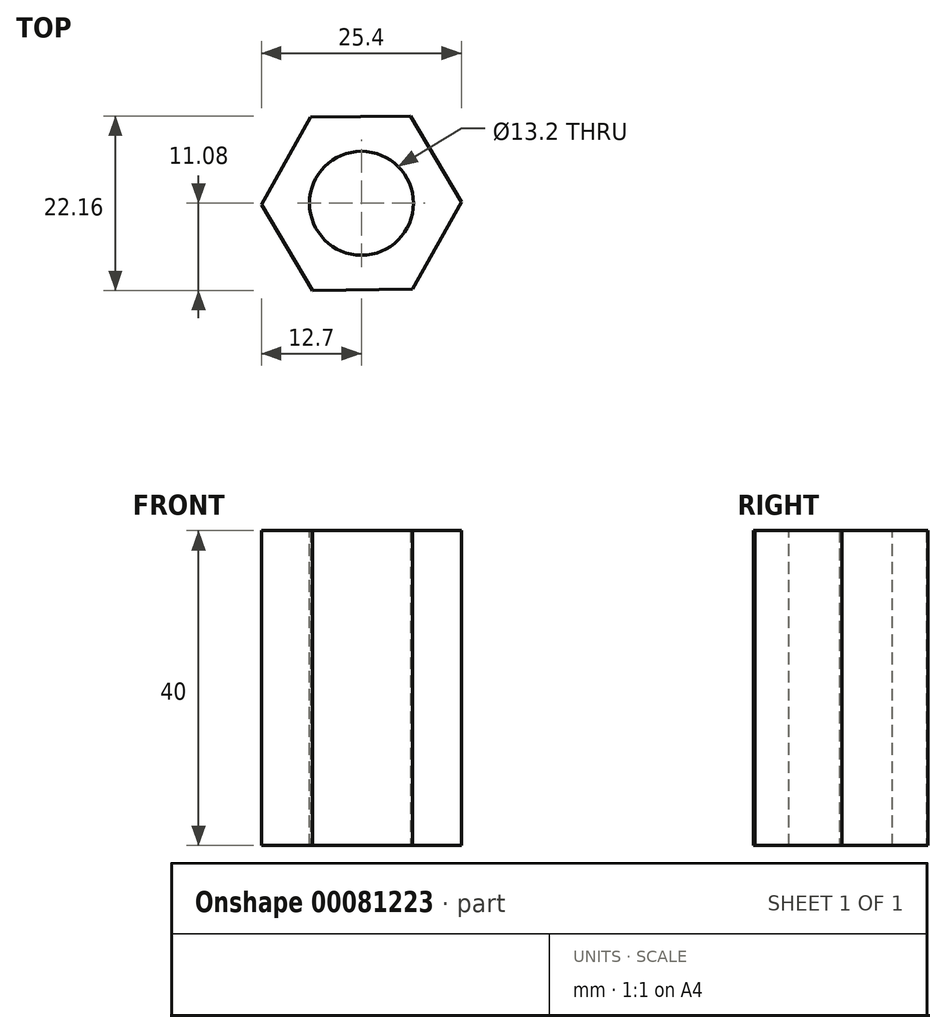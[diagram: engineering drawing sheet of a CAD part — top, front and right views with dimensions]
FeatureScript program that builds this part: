
annotation { "Feature Type Name" : "Feature", "Feature Type Description" : "" }
export const myFeature = defineFeature(function(context is Context, id is Id, definition is map)
    precondition{}
    {
        {
            var Q0;
            Q0=qCreatedBy(makeId("Top.planeOp"),FACE);
            var sketch = newSketch(context, id + "F0", { "sketchPlane" : qUnion([Q0])});
            skCircle(sketch, "E0.cCircle", {"center": v(0, 0) * mm, "radius": 11 * mm, "construction": true});
            skLineSegment(sketch, "E0.0", {"start": v(-12.7, -0.16) * mm, "end": v(-6.49, 10.92) * mm});
            skLineSegment(sketch, "E0.1", {"start": v(-6.49, 10.92) * mm, "end": v(6.21, 11.08) * mm});
            skLineSegment(sketch, "E0.2", {"start": v(6.21, 11.08) * mm, "end": v(12.7, 0.16) * mm});
            skLineSegment(sketch, "E0.3", {"start": v(12.7, 0.16) * mm, "end": v(6.49, -10.92) * mm});
            skLineSegment(sketch, "E0.4", {"start": v(6.49, -10.92) * mm, "end": v(-6.21, -11.08) * mm});
            skLineSegment(sketch, "E0.5", {"start": v(-6.21, -11.08) * mm, "end": v(-12.7, -0.16) * mm});
            skPoint(sketch, "E0.0.midPoint", {"position": v(-9.6, 5.38) * mm});
            skSolve(sketch);
        }
        {
            var Q0;
            Q0=makeQuery(id+"F0.imprint","IMPRINT",FACE,{"disambiguationData":[TD([[makeQuery(id+"F0.imprint","IMPRINT",EDGE,{"derivedFrom":sQuery(id+"F0.wireOp",EDGE,"E0.0")}),-1.0]])]});
            extrude(context, id + "F1", {"entities" : qUnion([Q0]), "depth" : 40 * mm});
        }
        {
            var Q0;
            Q0=sQuery(id+"F0.wireOp",VERTEX,"E0.cCircle.center");
            var Q1;
            Q1=makeQuery(id+"F1.opExtrude","SWEPT_BODY",BODY,{"disambiguationData":[OSD([sQuery(id+"F0.wireOp",EDGE,"E0.0"),sQuery(id+"F0.wireOp",EDGE,"E0.1"),sQuery(id+"F0.wireOp",EDGE,"E0.2"),sQuery(id+"F0.wireOp",EDGE,"E0.3"),sQuery(id+"F0.wireOp",EDGE,"E0.4"),sQuery(id+"F0.wireOp",EDGE,"E0.5")])]});
            hole(context, id + "F2", {"style" : HoleStyle.SIMPLE, "endStyle" : HoleEndStyle.THROUGH, "oppositeDirection" : true, "standardTappedOrClearance" : lookupTablePath({ "standard" : "ISO", "fit" : "Normal", "size" : "M12", "type" : "Clearance" }), "standardBlindInLast" : lookupTablePath({ "fit" : "Standard", "standard" : "ISO", "size" : "M12", "type" : "Clearance" }), "holeDiameter" : 13.2 * mm, "locations" : qUnion([Q0]), "scope" : qUnion([Q1]), "isTappedThrough" : true, "startStyle" : HoleStartStyle.PART});
        }
    });
